# Revit family: Gira_514200
name_source: partatom
category: Allgemeines Modell
revit_build: Autodesk Revit 2017 (Build: 20160225_1515(x64)
units: mm (PartAtom-declared; Revit-internal decimal feet)

## family parameters
Basisbauteil = Fläche
Beim Laden mit Abzugskörper schneiden = Nein
Bemaßung runder Anschluss = Durchmesser verwenden
Gemeinsam genutzt = Nein
Kann Basisbauteil für Bewehrung sein = Nein
Raumberechnungspunkt = Nein
Teiletyp = Normal

## types (1)
- Gira_514200
    BIM = https://media.stage.bim.site
    Beschreibung = KNX PB sens.3 Plus 2g Sys55,KNX pushbutton sensor 3 Plus 2-gang,System 55, Gira E22,Start-up rocker,Features:,- Mounting on bus coupler 3 or bus coupler 3 external sensor.,- Disassembly safeguard by screw connection.,- Backlit graphic display and various display possibilities, e.g. temperature, time, date, alarm texts, information texts.,- Two multicoloured status LEDs per operating surface.,- Multicoloured status LED (red, green, blue) can be parameterised via the ETS.,- Inscription space illumination for rocker sets with inscription space.,- Internal temperature sensor for measuring ambient room temperature.,Pushbutton sensor properties::,- Rocker or button function can be set for each operating surface.,- Rocker function: Switching, dimming, blind control, value transmitter 1-byte, value transmitter 2-byte, scene auxiliary unit, 2-channel operation and manual fan control.,- Button function: Switching, dimming, blind controller, value transmitter 1-byte, value transmitter 2-byte, scene auxiliary unit, 2-channel operation, controller auxiliary unit, controller operation, heater clock operation and manual fan control.,- Controller auxiliary unit or controller operation: Operating mode changeover, (defined selection of operating mode or switching between various operating modes with controller auxiliary unit), switching of presence condition, setpoint offset.,- Blocker for blocking individual button or rocker functions.,- Alarm message displayed through all LEDs flashing.,- Multicoloured status LED (red, green, blue) can be configured globally or separately. A superimposed function can be activated on the bus whereby the colour and display information of individual status LEDs can be modified according to priority.,- Illumination of inscription space ON, OFF, automatic switch-off, or switchable via object.,- Communication object for brightness control of status LED, illumination of inscription space and backlighting of display.,Room temperature controller properties::,- Operating modes: Comfort, standby, night, and frost or heat protection with their own temperature setpoint values (for heating and or cooling).,- Comfort extension using the presence button.,- Frost or heat protection changeover via window status or via frost protection automatic function.,- Room temperature controller information is shown in the device display.,- Either one or two control circuits.,- Various control types can be configured according to the heating or cooling level: PI control (constant or switching PWM) or 2-point control (switching).,- Control parameters for PI controllers and 2-point controllers can be set.,- Internal temperature sensor and up to two external temperature sensors (1 x object, 1 x wired) possible for room temperature measurement.,- Optional external wired remote sensor for floor heating.,- Heating clock with 28 switching times.,LC display properties::,- Graphic display with switchable LED backlighting.,- 1-range or 2-range display.,- Text information in the display in the languages: German, English, Dutch, Norwegian, Russian and Polish. Other languages are available on the Internet.,,Notes :,- Professional labelling with the Gira Inscription Service www.marking.gira.com.,- The pushbutton sensor is supplied with a program-neutral start-up rocker. The suitable rocker set for the design line must be ordered separately.
    Bus connection included = Nein
    Bus system KNX = Ja
    Bus system KNX radio = Nein
    Bus system LON = Nein
    Bus system Powernet = Nein
    Bus system radio frequent = Nein
    Colour = Other
    Data sheet = https://katalog.gira.de
    Degree of protection (IP) = IP20
    GTIN = 4010337086888
    HAN = 514200
    Hersteller = Gira
    Material = Other
    Material quality = Other
    Mounting method = Flush mounted (plaster)
    Number of actuation points = 6
    Number of buttons = 2
    Other bus systems = None
    Productwebsite = http://katalog.gira.de
    Surface finishing = Not applicable
    Surface protection = Other
    Transparent = Nein
    Typname = KNX PB sens.3 Plus 2-g System 55, Gira E22
    URL = https://www.gira.de
    Vorgabe-Ansicht = 1219 mm
    With IR sensor = Nein
    With LED indication = Ja
    With anti-theft/dismantling protection = Ja
    With display = Ja
    With label area = Nein
    With room temperature controller = Ja

## geometry (parser evidence)
native form markers: Sweep x2
no freeform markers — native parametric forms only
